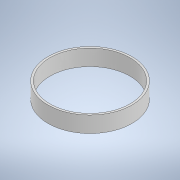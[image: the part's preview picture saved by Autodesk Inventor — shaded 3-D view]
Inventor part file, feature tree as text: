
AUTODESK INVENTOR PART (.ipt)
format: ipt  version: 2021 (Build 250183000, 183)  size: 104,448 bytes
history: native  units: mm
features: extrude x2, sketch x2
ambient origin geometry x8: Origin, YZ Plane, XZ Plane, XY Plane, X Axis, Y Axis, Z Axis, Center Point
bodies: Body1 (feature_tree)
feature tree (4):
  extrude  "Extrusion1"  Depth=21.0mm
  extrude  "Extrusion2"  Depth=4.0mm TaperAngle=0.0deg
  sketch  "Esquisse1"
  sketch  "Esquisse3"
